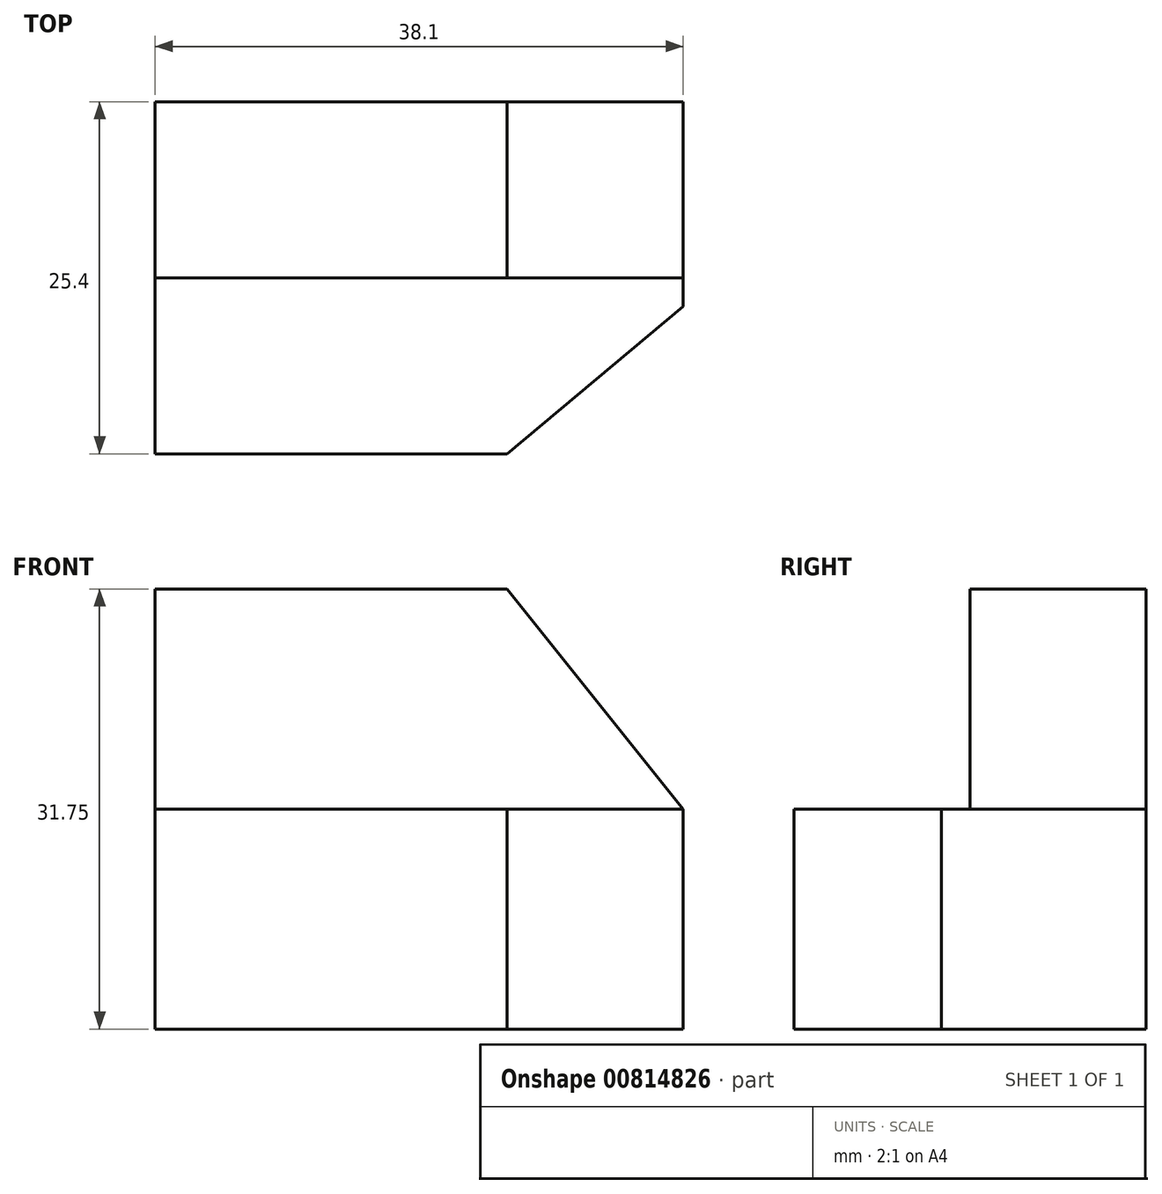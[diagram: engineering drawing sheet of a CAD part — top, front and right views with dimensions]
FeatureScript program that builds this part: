
annotation { "Feature Type Name" : "Feature", "Feature Type Description" : "" }
export const myFeature = defineFeature(function(context is Context, id is Id, definition is map)
    precondition{}
    {
        {
            var Q0;
            Q0=qCreatedBy(makeId("Top.planeOp"),FACE);
            var sketch = newSketch(context, id + "F0", { "sketchPlane" : qUnion([Q0])});
            skLineSegment(sketch, "E0", {"start": v(0, 0) * mm, "end": v(38.1, 0) * mm});
            skLineSegment(sketch, "E1", {"start": v(38.1, 0) * mm, "end": v(38.1, 25.4) * mm});
            skLineSegment(sketch, "E2", {"start": v(38.1, 25.4) * mm, "end": v(0, 25.4) * mm});
            skLineSegment(sketch, "E3", {"start": v(0, 25.4) * mm, "end": v(0, 0) * mm});
            skSolve(sketch);
        }
        {
            var Q0;
            Q0 = qSketchRegion(id + "F0", true);
            extrude(context, id + "F1", {"entities" : qUnion([Q0]), "depth" : 31.75 * mm, "offsetDistance" : 25.4 * mm});
        }
        {
            var Q0;
            Q0=makeQuery(id+"F1.opExtrude","SWEPT_FACE",FACE,{"disambiguationData":[OSD([sQuery(id+"F0.wireOp",EDGE,"E0")])]});
            var sketch = newSketch(context, id + "F2", { "sketchPlane" : qUnion([Q0])});
            skLineSegment(sketch, "E4", {"start": v(0, 31.75) * mm, "end": v(0, 15.88) * mm});
            skLineSegment(sketch, "E5", {"start": v(0, 15.88) * mm, "end": v(38.1, 15.88) * mm});
            skLineSegment(sketch, "E6", {"start": v(38.1, 15.88) * mm, "end": v(38.1, 31.75) * mm});
            skLineSegment(sketch, "E7", {"start": v(38.1, 31.75) * mm, "end": v(0, 31.75) * mm});
            skSolve(sketch);
        }
        {
            var Q0;
            Q0=makeQuery(id+"F2.imprint","IMPRINT",FACE,{"disambiguationData":[TD([[makeQuery(id+"F2.imprint","IMPRINT",EDGE,{"derivedFrom":sQuery(id+"F2.wireOp",EDGE,"E4")}),1.0]])]});
            extrude(context, id + "F3", {"entities" : qUnion([Q0]), "operationType" : NewBodyOperationType.REMOVE, "oppositeDirection" : true, "depth" : 12.7 * mm, "offsetDistance" : 25.4 * mm});
        }
        {
            var Q0;
            Q0=makeQuery(id+"F3.boolean.opBoolean","COPY",FACE,{"derivedFrom":makeQuery(id+"F3.opExtrude","CAP_FACE",FACE,{"disambiguationData":[OSD([sQuery(id+"F2.wireOp",EDGE,"E4"),sQuery(id+"F2.wireOp",EDGE,"E5"),sQuery(id+"F2.wireOp",EDGE,"E6"),sQuery(id+"F2.wireOp",EDGE,"E7")])],"isStart":false})});
            var sketch = newSketch(context, id + "F4", { "sketchPlane" : qUnion([Q0])});
            skLineSegment(sketch, "E8", {"start": v(38.1, 31.75) * mm, "end": v(25.4, 31.75) * mm});
            skLineSegment(sketch, "E9", {"start": v(25.4, 31.75) * mm, "end": v(38.1, 15.88) * mm});
            skLineSegment(sketch, "E10", {"start": v(38.1, 15.88) * mm, "end": v(38.1, 31.75) * mm});
            skSolve(sketch);
        }
        {
            var Q0;
            Q0 = qSketchRegion(id + "F4", true);
            extrude(context, id + "F5", {"entities" : qUnion([Q0]), "operationType" : NewBodyOperationType.REMOVE, "oppositeDirection" : true, "depth" : 25.4 * mm, "offsetDistance" : 25.4 * mm});
        }
        {
            var Q0;
            Q0=makeQuery(id+"F1.opExtrude","CAP_FACE",FACE,{"disambiguationData":[OSD([sQuery(id+"F0.wireOp",EDGE,"E0"),sQuery(id+"F0.wireOp",EDGE,"E1"),sQuery(id+"F0.wireOp",EDGE,"E2"),sQuery(id+"F0.wireOp",EDGE,"E3")])],"isStart":true});
            var sketch = newSketch(context, id + "F6", { "sketchPlane" : qUnion([Q0])});
            skLineSegment(sketch, "E11", {"start": v(38.1, 0) * mm, "end": v(25.4, 0) * mm});
            skLineSegment(sketch, "E12", {"start": v(25.4, 0) * mm, "end": v(38.1, -10.63) * mm});
            skLineSegment(sketch, "E13", {"start": v(38.1, -10.63) * mm, "end": v(38.1, 0) * mm});
            skSolve(sketch);
        }
        {
            var Q0;
            Q0 = qSketchRegion(id + "F6", true);
            extrude(context, id + "F7", {"entities" : qUnion([Q0]), "operationType" : NewBodyOperationType.REMOVE, "oppositeDirection" : true, "depth" : 25.4 * mm, "offsetDistance" : 25.4 * mm});
        }
    });
